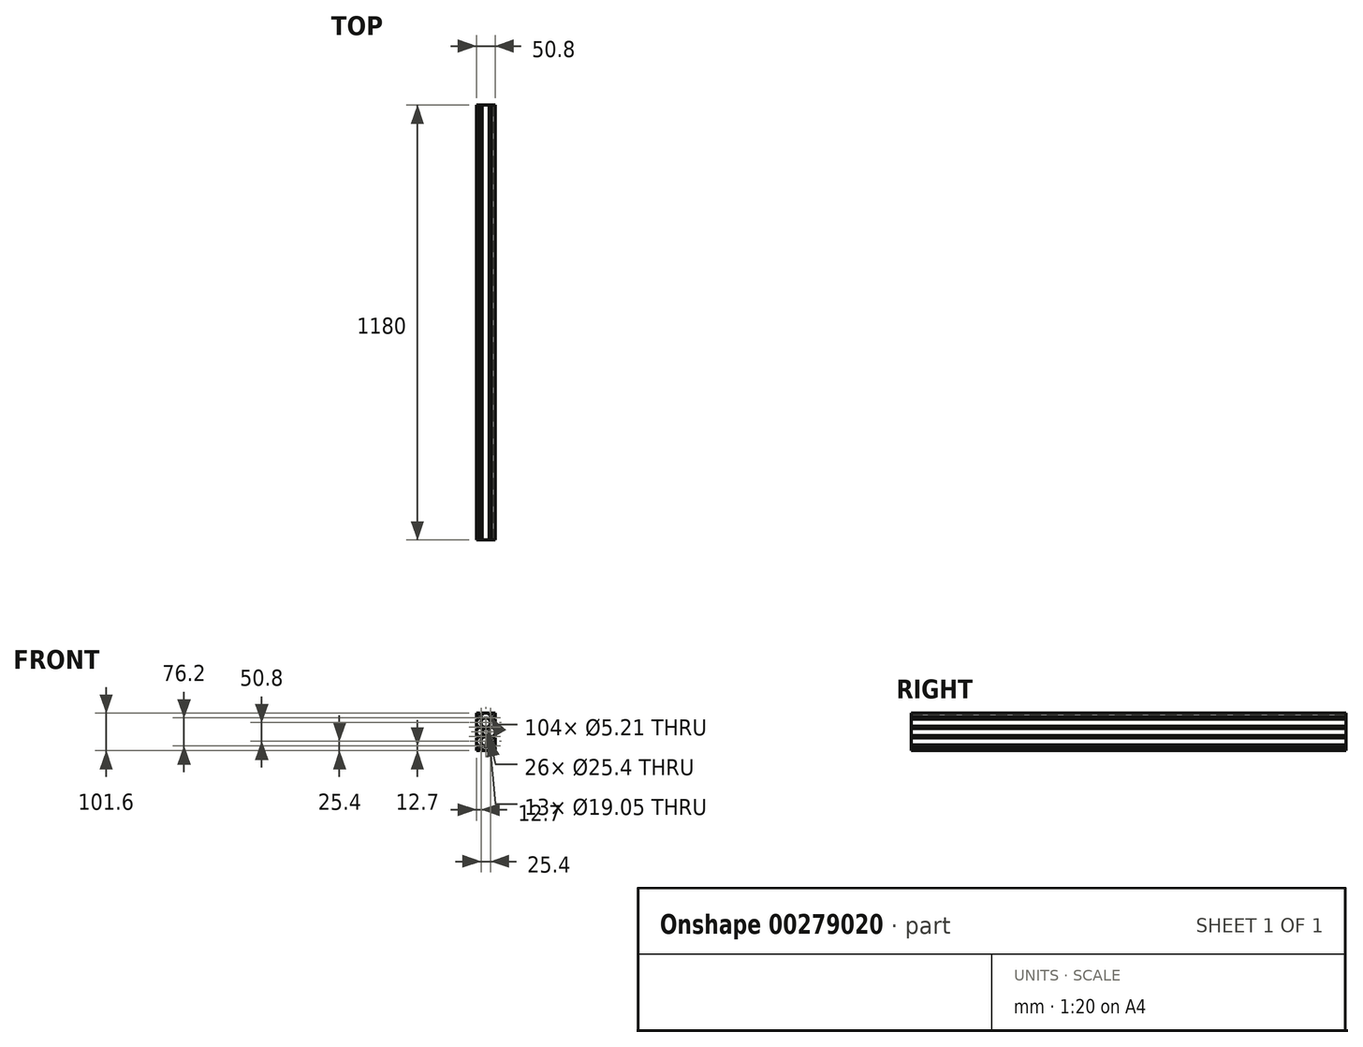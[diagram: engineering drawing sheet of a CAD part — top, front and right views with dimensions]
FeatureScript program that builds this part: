
annotation { "Feature Type Name" : "Feature", "Feature Type Description" : "" }
export const myFeature = defineFeature(function(context is Context, id is Id, definition is map)
    precondition{}
    {
        {
            var Q0;
            Q0=qCreatedBy(makeId("Front.planeOp"),FACE);
            var sketch = newSketch(context, id + "F0", { "sketchPlane" : qUnion([Q0])});
            skLineSegment(sketch, "E0.bottom", {"start": v(25.4, -50.8) * mm, "end": v(15.88, -50.8) * mm});
            skLineSegment(sketch, "E0.top", {"start": v(25.4, 50.8) * mm, "end": v(15.88, 50.8) * mm});
            skLineSegment(sketch, "E0.left", {"start": v(25.4, -50.8) * mm, "end": v(25.4, -41.27) * mm});
            skLineSegment(sketch, "E0.right", {"start": v(-25.4, -50.8) * mm, "end": v(-25.4, -41.27) * mm});
            skPoint(sketch, "E0.middle", {"position": v(0, 0) * mm});
            skLineSegment(sketch, "E1.0", {"start": v(-15.88, -50.8) * mm, "end": v(-15.87, 50.8) * mm, "construction": true});
            skLineSegment(sketch, "E2.0", {"start": v(15.88, -50.8) * mm, "end": v(15.88, 50.8) * mm, "construction": true});
            skLineSegment(sketch, "E3.0", {"start": v(34.18, 41.28) * mm, "end": v(-31.96, 41.27) * mm, "construction": true});
            skLineSegment(sketch, "E4.0", {"start": v(41.78, -41.27) * mm, "end": v(-39.13, -41.28) * mm, "construction": true});
            skLineSegment(sketch, "E5", {"start": v(-15.88, -50.8) * mm, "end": v(-15.88, -44.45) * mm});
            skLineSegment(sketch, "E6", {"start": v(-15.88, -44.45) * mm, "end": v(-9.52, -44.45) * mm});
            skLineSegment(sketch, "E7", {"start": v(-9.52, -44.45) * mm, "end": v(-9.52, -50.8) * mm});
            skLineSegment(sketch, "E8", {"start": v(15.88, -50.8) * mm, "end": v(15.88, -44.45) * mm});
            skLineSegment(sketch, "E9", {"start": v(15.88, -44.45) * mm, "end": v(9.53, -44.45) * mm});
            skLineSegment(sketch, "E10", {"start": v(9.53, -44.45) * mm, "end": v(9.53, -50.8) * mm});
            skLineSegment(sketch, "E11", {"start": v(-61.96, 0) * mm, "end": v(55.32, 0) * mm, "construction": true});
            skPoint(sketch, "E11.endSnap0", {"position": v(25.4, 0) * mm});
            skLineSegment(sketch, "E12.MirrorCS", {"start": v(15.88, 44.45) * mm, "end": v(9.53, 44.45) * mm});
            skLineSegment(sketch, "E13.MirrorCS", {"start": v(9.53, 44.45) * mm, "end": v(9.53, 50.8) * mm});
            skLineSegment(sketch, "E14.MirrorCS", {"start": v(-9.52, 44.45) * mm, "end": v(-9.52, 50.8) * mm});
            skLineSegment(sketch, "E15.MirrorCS", {"start": v(-15.88, 44.45) * mm, "end": v(-9.52, 44.45) * mm});
            skLineSegment(sketch, "E16.MirrorCS", {"start": v(-15.88, 50.8) * mm, "end": v(-15.88, 44.45) * mm});
            skLineSegment(sketch, "E17.MirrorCS", {"start": v(15.88, 50.8) * mm, "end": v(15.88, 44.45) * mm});
            skLineSegment(sketch, "E18", {"start": v(25.4, -41.27) * mm, "end": v(19.05, -41.27) * mm});
            skLineSegment(sketch, "E19", {"start": v(19.05, -41.27) * mm, "end": v(19.05, -34.92) * mm});
            skLineSegment(sketch, "E20", {"start": v(19.05, -34.92) * mm, "end": v(25.4, -34.92) * mm});
            skLineSegment(sketch, "E21.0", {"start": v(19.05, -15.87) * mm, "end": v(25.4, -15.87) * mm});
            skLineSegment(sketch, "E22", {"start": v(19.05, -15.87) * mm, "end": v(19.05, -9.52) * mm});
            skLineSegment(sketch, "E23", {"start": v(19.05, -9.52) * mm, "end": v(25.4, -9.52) * mm});
            skLineSegment(sketch, "E24.0", {"start": v(19.05, 9.53) * mm, "end": v(25.4, 9.53) * mm});
            skLineSegment(sketch, "E25", {"start": v(19.05, 9.53) * mm, "end": v(19.05, 15.88) * mm});
            skLineSegment(sketch, "E26", {"start": v(25.4, 41.28) * mm, "end": v(19.05, 41.28) * mm});
            skLineSegment(sketch, "E27", {"start": v(19.05, 41.28) * mm, "end": v(19.05, 34.93) * mm});
            skLineSegment(sketch, "E28", {"start": v(19.05, 34.93) * mm, "end": v(25.4, 34.93) * mm});
            skLineSegment(sketch, "E29", {"start": v(19.05, 15.88) * mm, "end": v(25.4, 15.88) * mm});
            skLineSegment(sketch, "E30", {"start": v(0, -19.99) * mm, "end": v(0, 20) * mm, "construction": true});
            skLineSegment(sketch, "E31.MirrorCS", {"start": v(-19.05, 34.93) * mm, "end": v(-25.4, 34.93) * mm});
            skLineSegment(sketch, "E32.MirrorCS", {"start": v(-19.05, 41.28) * mm, "end": v(-19.05, 34.93) * mm});
            skLineSegment(sketch, "E33.MirrorCS", {"start": v(-19.05, 15.88) * mm, "end": v(-25.4, 15.88) * mm});
            skLineSegment(sketch, "E34.MirrorCS", {"start": v(-19.05, 9.53) * mm, "end": v(-25.4, 9.53) * mm});
            skLineSegment(sketch, "E35.MirrorCS", {"start": v(-19.05, 9.53) * mm, "end": v(-19.05, 15.88) * mm});
            skLineSegment(sketch, "E36.MirrorCS", {"start": v(-19.05, -15.87) * mm, "end": v(-25.4, -15.87) * mm});
            skLineSegment(sketch, "E37.MirrorCS", {"start": v(-19.05, -15.87) * mm, "end": v(-19.05, -9.52) * mm});
            skLineSegment(sketch, "E38.MirrorCS", {"start": v(-19.05, -9.52) * mm, "end": v(-25.4, -9.52) * mm});
            skLineSegment(sketch, "E39.MirrorCS", {"start": v(-19.05, -41.27) * mm, "end": v(-19.05, -34.92) * mm});
            skLineSegment(sketch, "E40.MirrorCS", {"start": v(-19.05, -34.92) * mm, "end": v(-25.4, -34.92) * mm});
            skLineSegment(sketch, "E41", {"start": v(-19.05, 41.28) * mm, "end": v(-25.4, 41.28) * mm});
            skLineSegment(sketch, "E42", {"start": v(-19.05, -41.27) * mm, "end": v(-25.4, -41.27) * mm});
            skLineSegment(sketch, "E43.0", {"start": v(25.4, 38.1) * mm, "end": v(-25.4, 38.1) * mm, "construction": true});
            skLineSegment(sketch, "E44.0", {"start": v(25.4, -38.1) * mm, "end": v(-25.4, -38.1) * mm, "construction": true});
            skLineSegment(sketch, "E45.0", {"start": v(12.7, -50.8) * mm, "end": v(12.7, 50.8) * mm, "construction": true});
            skLineSegment(sketch, "E46.0", {"start": v(-12.7, -50.8) * mm, "end": v(-12.7, 50.8) * mm, "construction": true});
            skCircle(sketch, "E47", {"center": v(-12.7, -38.1) * mm, "radius": 2.6 * mm});
            skCircle(sketch, "E48", {"center": v(12.7, -38.1) * mm, "radius": 2.6 * mm});
            skCircle(sketch, "E49", {"center": v(-12.7, 38.1) * mm, "radius": 2.6 * mm});
            skCircle(sketch, "E50", {"center": v(12.7, 38.1) * mm, "radius": 2.6 * mm});
            skCircle(sketch, "E51", {"center": v(-12.7, 12.7) * mm, "radius": 2.6 * mm});
            skPoint(sketch, "E51.centerSnap0", {"position": v(-19.05, 12.7) * mm});
            skCircle(sketch, "E52", {"center": v(12.7, 12.7) * mm, "radius": 2.6 * mm});
            skPoint(sketch, "E52.centerSnap0", {"position": v(19.05, 12.7) * mm});
            skCircle(sketch, "E53", {"center": v(-12.7, -12.7) * mm, "radius": 2.6 * mm});
            skPoint(sketch, "E53.centerSnap0", {"position": v(-19.05, -12.7) * mm});
            skCircle(sketch, "E54", {"center": v(12.7, -12.7) * mm, "radius": 2.6 * mm});
            skPoint(sketch, "E54.centerSnap0", {"position": v(19.05, -12.7) * mm});
            skLineSegment(sketch, "E55", {"start": v(-22.23, -15.87) * mm, "end": v(-22.23, -34.92) * mm, "construction": true});
            skLineSegment(sketch, "E56", {"start": v(-25.4, -25.4) * mm, "end": v(25.4, -25.4) * mm, "construction": true});
            skPoint(sketch, "E56.startSnap0", {"position": v(-22.23, -25.4) * mm});
            skCircle(sketch, "E57", {"center": v(0, -25.4) * mm, "radius": 12.7 * mm});
            skLineSegment(sketch, "E58", {"start": v(-22.23, 34.93) * mm, "end": v(-22.23, 15.88) * mm, "construction": true});
            skLineSegment(sketch, "E59", {"start": v(-25.4, 25.4) * mm, "end": v(25.4, 25.4) * mm, "construction": true});
            skPoint(sketch, "E59.startSnap0", {"position": v(-22.23, 25.4) * mm});
            skCircle(sketch, "E60", {"center": v(0, 25.4) * mm, "radius": 12.7 * mm});
            skCircle(sketch, "E61", {"center": v(0, 0) * mm, "radius": 9.53 * mm});
            skLineSegment(sketch, "E62.trimOffspring", {"start": v(9.53, 50.8) * mm, "end": v(-9.52, 50.8) * mm});
            skLineSegment(sketch, "E63.trimOffspring", {"start": v(-15.88, 50.8) * mm, "end": v(-25.4, 50.8) * mm});
            skLineSegment(sketch, "E64.trimOffspring", {"start": v(-25.4, 41.28) * mm, "end": v(-25.4, 50.8) * mm});
            skLineSegment(sketch, "E65.trimOffspring", {"start": v(25.4, 41.28) * mm, "end": v(25.4, 50.8) * mm});
            skLineSegment(sketch, "E66.trimOffspring", {"start": v(25.4, 15.88) * mm, "end": v(25.4, 34.93) * mm});
            skLineSegment(sketch, "E67.trimOffspring", {"start": v(-25.4, 15.88) * mm, "end": v(-25.4, 34.93) * mm});
            skLineSegment(sketch, "E68.trimOffspring", {"start": v(25.4, -9.52) * mm, "end": v(25.4, 9.53) * mm});
            skLineSegment(sketch, "E69.trimOffspring", {"start": v(-25.4, -9.52) * mm, "end": v(-25.4, 9.53) * mm});
            skLineSegment(sketch, "E70.trimOffspring", {"start": v(25.4, -34.92) * mm, "end": v(25.4, -15.87) * mm});
            skLineSegment(sketch, "E71.trimOffspring", {"start": v(-25.4, -34.92) * mm, "end": v(-25.4, -15.87) * mm});
            skLineSegment(sketch, "E72.trimOffspring", {"start": v(-15.88, -50.8) * mm, "end": v(-25.4, -50.8) * mm});
            skLineSegment(sketch, "E73.trimOffspring", {"start": v(9.53, -50.8) * mm, "end": v(-9.52, -50.8) * mm});
            skSolve(sketch);
        }
        {
            var Q0;
            Q0=makeQuery(id+"F0.imprint","IMPRINT",FACE,{"disambiguationData":[TD([[makeQuery(id+"F0.imprint","IMPRINT",EDGE,{"derivedFrom":sQuery(id+"F0.wireOp",EDGE,"E0.bottom")}),-1.0]])]});
            extrude(context, id + "F1", {"entities" : qUnion([Q0]), "endBound" : BoundingType.SYMMETRIC, "depth" : 1180 * mm});
        }
    });
